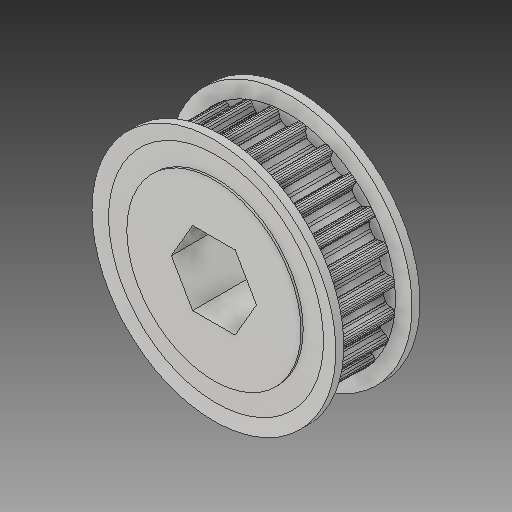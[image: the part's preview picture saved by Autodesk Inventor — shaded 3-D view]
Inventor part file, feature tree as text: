
AUTODESK INVENTOR PART (.ipt)
format: ipt  version: 2017 (Build 210142000, 142)  size: 701,952 bytes
history: native  units: in
note: dims shown in document units (in); Inventor stores cm internally (conversion verified against a paired STEP export)
features: mirror x1
ambient origin geometry x8: Origin, YZ Plane, XZ Plane, XY Plane, X Axis, Y Axis, Z Axis, Center Point
bodies: Solid1 (feature_tree)
feature tree (1):
  mirror  "Mirror1"
